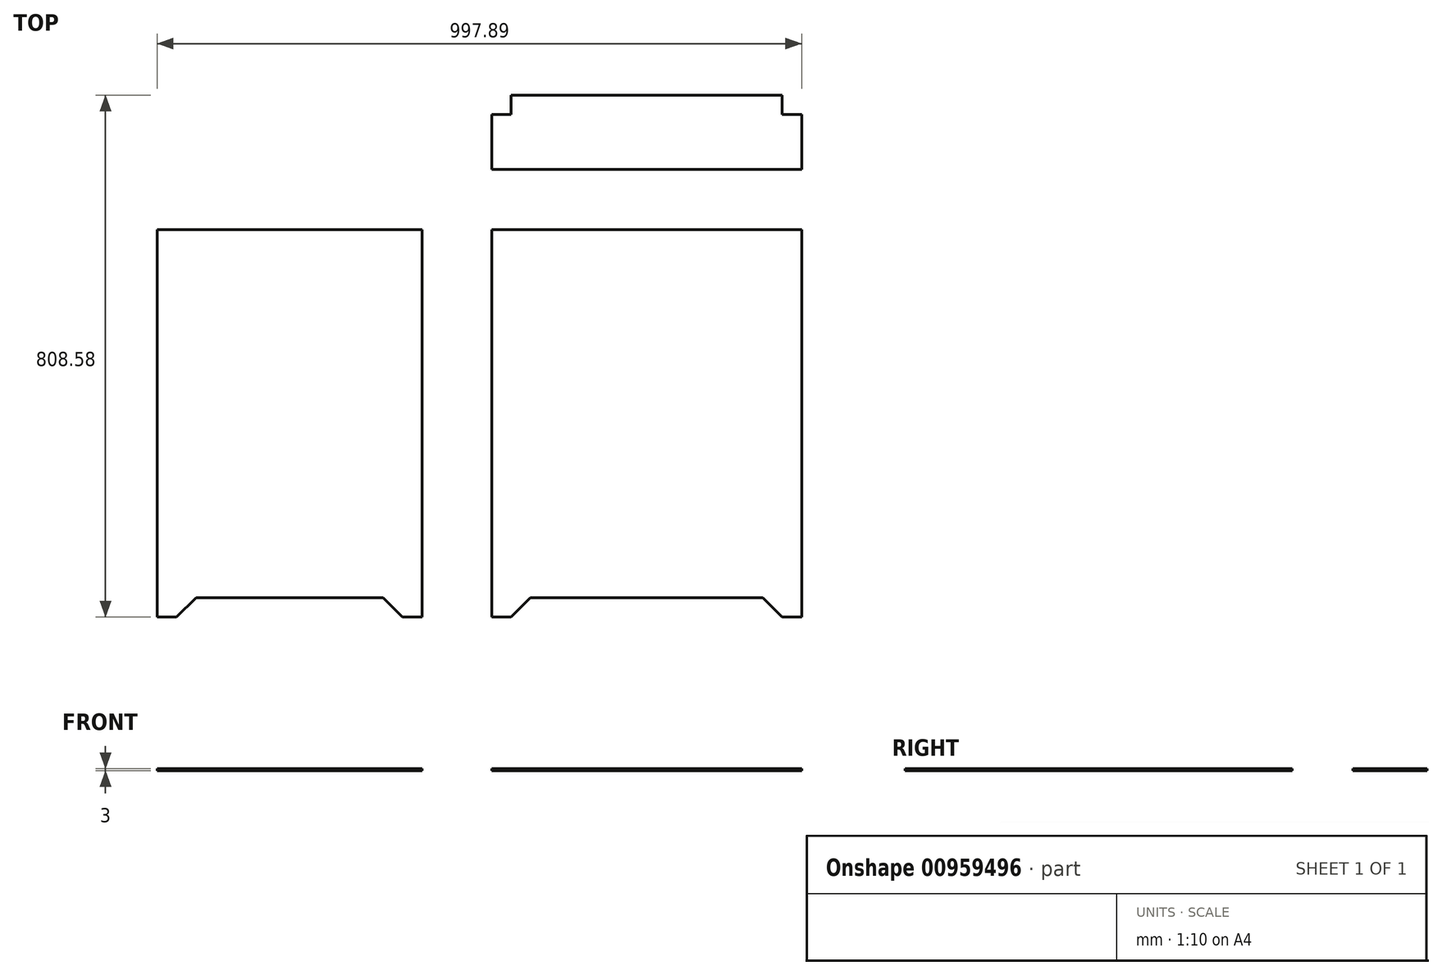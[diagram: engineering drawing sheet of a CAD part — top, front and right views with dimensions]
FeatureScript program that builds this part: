
annotation { "Feature Type Name" : "Feature", "Feature Type Description" : "" }
export const myFeature = defineFeature(function(context is Context, id is Id, definition is map)
    precondition{}
    {
        {
            var Q0;
            Q0=qCreatedBy(makeId("Top.planeOp"),FACE);
            var sketch = newSketch(context, id + "F0", { "sketchPlane" : qUnion([Q0])});
            skLineSegment(sketch, "E0.bottom", {"start": v(205, -300) * mm, "end": v(175, -300) * mm});
            skLineSegment(sketch, "E0.top", {"start": v(205, 300) * mm, "end": v(-205, 300) * mm});
            skLineSegment(sketch, "E0.left", {"start": v(205, -300) * mm, "end": v(205, 300) * mm});
            skLineSegment(sketch, "E0.right", {"start": v(-205, -300) * mm, "end": v(-205, 300) * mm});
            skPoint(sketch, "E0.middle", {"position": v(0, 0) * mm});
            skLineSegment(sketch, "E1", {"start": v(-175, -300) * mm, "end": v(-145, -270) * mm});
            skLineSegment(sketch, "E2", {"start": v(-145, -270) * mm, "end": v(145, -270) * mm});
            skLineSegment(sketch, "E3", {"start": v(145, -270) * mm, "end": v(175, -300) * mm});
            skLineSegment(sketch, "E4.trimOffspring", {"start": v(-175, -300) * mm, "end": v(-205, -300) * mm});
            skSolve(sketch);
        }
        {
            var Q0;
            Q0=qCreatedBy(makeId("Top.planeOp"),FACE);
            var sketch = newSketch(context, id + "F1", { "sketchPlane" : qUnion([Q0])});
            skLineSegment(sketch, "E5.bottom", {"start": v(312.9, -300) * mm, "end": v(342.9, -300) * mm});
            skLineSegment(sketch, "E5.top", {"start": v(312.9, 300) * mm, "end": v(792.9, 300) * mm});
            skLineSegment(sketch, "E5.left", {"start": v(312.9, -300) * mm, "end": v(312.9, 300) * mm});
            skLineSegment(sketch, "E5.right", {"start": v(792.9, -300) * mm, "end": v(792.9, 300) * mm});
            skPoint(sketch, "E5.middle", {"position": v(552.9, 0) * mm});
            skLineSegment(sketch, "E6", {"start": v(342.9, -300) * mm, "end": v(372.9, -270) * mm});
            skLineSegment(sketch, "E7", {"start": v(372.9, -270) * mm, "end": v(732.9, -270) * mm});
            skLineSegment(sketch, "E8", {"start": v(732.9, -270) * mm, "end": v(762.9, -300) * mm});
            skLineSegment(sketch, "E9.trimOffspring", {"start": v(762.9, -300) * mm, "end": v(792.9, -300) * mm});
            skSolve(sketch);
        }
        {
            var Q0;
            Q0=qCreatedBy(makeId("Top.planeOp"),FACE);
            var sketch = newSketch(context, id + "F2", { "sketchPlane" : qUnion([Q0])});
            skLineSegment(sketch, "E10.bottom", {"start": v(792.9, 393.58) * mm, "end": v(312.9, 393.58) * mm});
            skLineSegment(sketch, "E10.top", {"start": v(762.9, 508.58) * mm, "end": v(342.9, 508.58) * mm});
            skLineSegment(sketch, "E10.left", {"start": v(792.9, 393.58) * mm, "end": v(792.9, 478.58) * mm});
            skLineSegment(sketch, "E10.right", {"start": v(312.9, 393.58) * mm, "end": v(312.9, 478.58) * mm});
            skPoint(sketch, "E10.middle", {"position": v(552.9, 451.08) * mm});
            skLineSegment(sketch, "E11", {"start": v(312.9, 478.58) * mm, "end": v(342.9, 478.58) * mm});
            skLineSegment(sketch, "E12", {"start": v(342.9, 478.58) * mm, "end": v(342.9, 508.58) * mm});
            skLineSegment(sketch, "E13", {"start": v(762.9, 508.58) * mm, "end": v(762.9, 478.58) * mm});
            skLineSegment(sketch, "E14", {"start": v(762.9, 478.58) * mm, "end": v(792.9, 478.58) * mm});
            skPoint(sketch, "E15.orphan", {"position": v(312.9, 393.58) * mm});
            skPoint(sketch, "E16.orphan", {"position": v(312.9, 508.58) * mm});
            skPoint(sketch, "E17.orphan", {"position": v(792.9, 508.58) * mm});
            skPoint(sketch, "E18.orphan", {"position": v(792.9, 393.58) * mm});
            skPoint(sketch, "E19.0", {"position": v(312.9, 300) * mm});
            skPoint(sketch, "E20.0", {"position": v(792.9, 300) * mm});
            skSolve(sketch);
        }
        {
            var Q0;
            Q0 = qSketchRegion(id + "F0", true);
            var Q1;
            Q1 = qSketchRegion(id + "F1", true);
            var Q2;
            Q2 = qSketchRegion(id + "F2", true);
            extrude(context, id + "F3", {"entities" : qUnion([Q0, Q1, Q2]), "depth" : 3 * mm, "offsetDistance" : 25 * mm});
        }
    });
